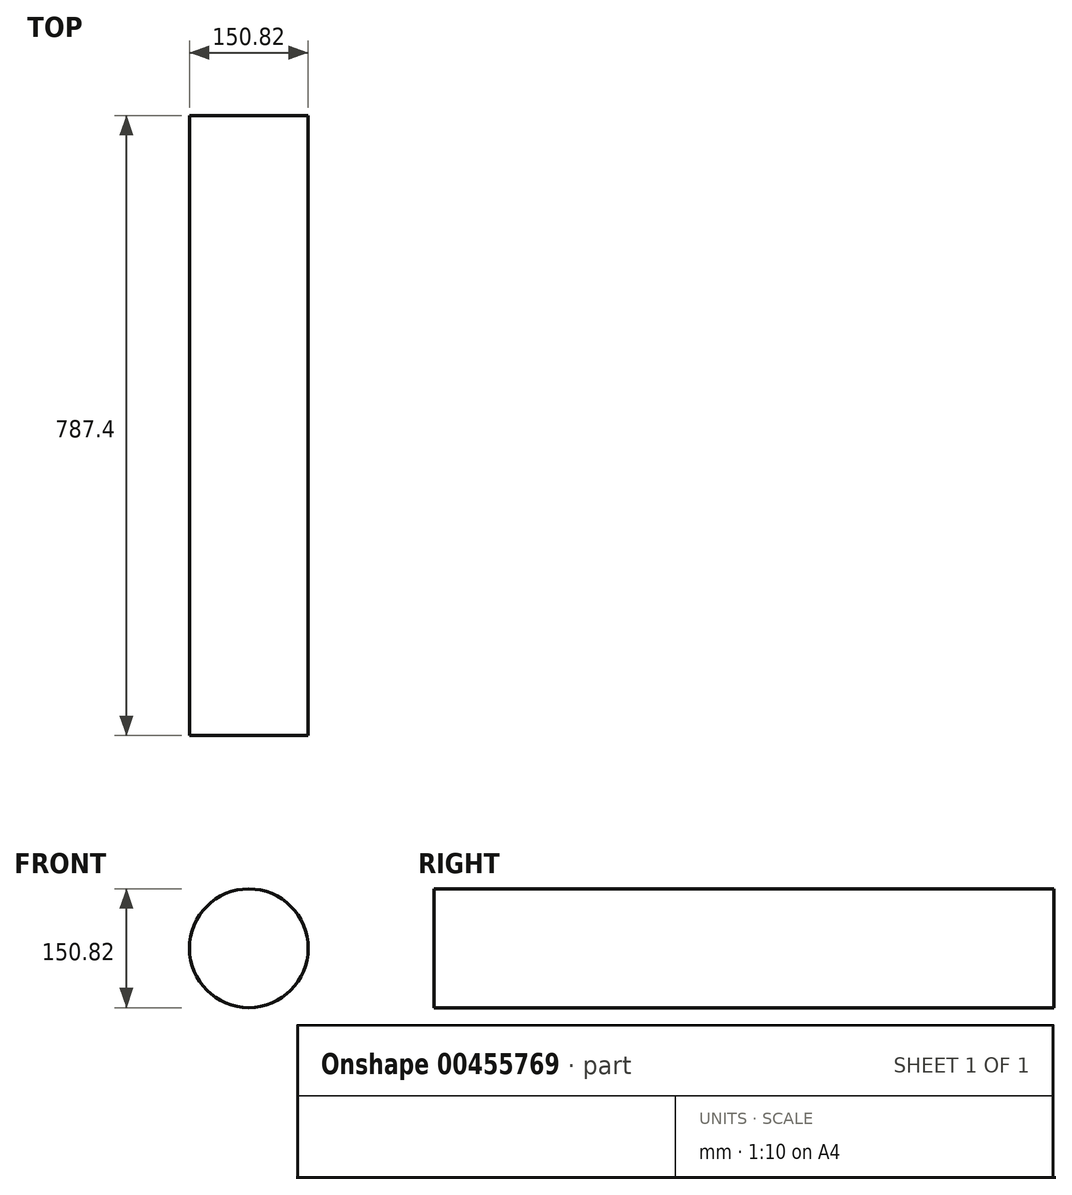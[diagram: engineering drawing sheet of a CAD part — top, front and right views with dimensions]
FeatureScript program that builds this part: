
annotation { "Feature Type Name" : "Feature", "Feature Type Description" : "" }
export const myFeature = defineFeature(function(context is Context, id is Id, definition is map)
    precondition{}
    {
        {
            var Q0;
            Q0=qCreatedBy(makeId("Front.planeOp"),FACE);
            var sketch = newSketch(context, id + "F0", { "sketchPlane" : qUnion([Q0])});
            skCircle(sketch, "E0", {"center": v(0, 0) * mm, "radius": 75.41 * mm});
            skSolve(sketch);
        }
        {
            var Q0;
            Q0 = qSketchRegion(id + "F0", true);
            extrude(context, id + "F1", {"entities" : qUnion([Q0]), "oppositeDirection" : true, "depth" : 787.4 * mm});
        }
    });
